# Revit family: BC_Aircalo_Fun40-IU-droite_LOD400_2019
name_source: partatom
category: Equipement de génie climatique
units: mm (PartAtom-declared; Revit-internal decimal feet)

## family parameters
Basée sur le plan de construction = Non
Cote de connecteur circulaire = Utiliser le diamètre
Couper avec des vides une fois chargée = Non
Numéro OmniClass = 23.75.70.17.27
Partagée = Non
Point de calcul de pièce = Non
Titre OmniClass = Fan Coil Units
Toujours verticalement = Non
Type d'élément = Normal

## types (1)
- FUN 30 I Std - Servitude Droite
    Body Material = Body Material
    Commentaires du type = FUN 30 I Std - Servitude Droite
    Connection Diameter = 13 mm
    Description = Version Revit 2019
    Exhaust air diameter = 200 mm
    Fabricant = Aircalo
    Galvenized Material = Galvanized
    Insulation Material = Polyurethane foam fireproof
    Main Material = Galvanized steel
    Mass = 15.00 kg
    Modèle = Ventilo-convecteur gainable FUN 30
    Motor power absorbed = 137 W
    Nominal Voltage = 230 V
    Outlet Diameter = 16 mm
    Overall Height = 237 mm
    Overall Length = 870 mm
    Overall Width = 716 mm
    Power Material = Power Material
    Service Area Material = Service Area

## geometry (parser evidence)
native form markers: Sweep x4
no freeform markers — native parametric forms only
